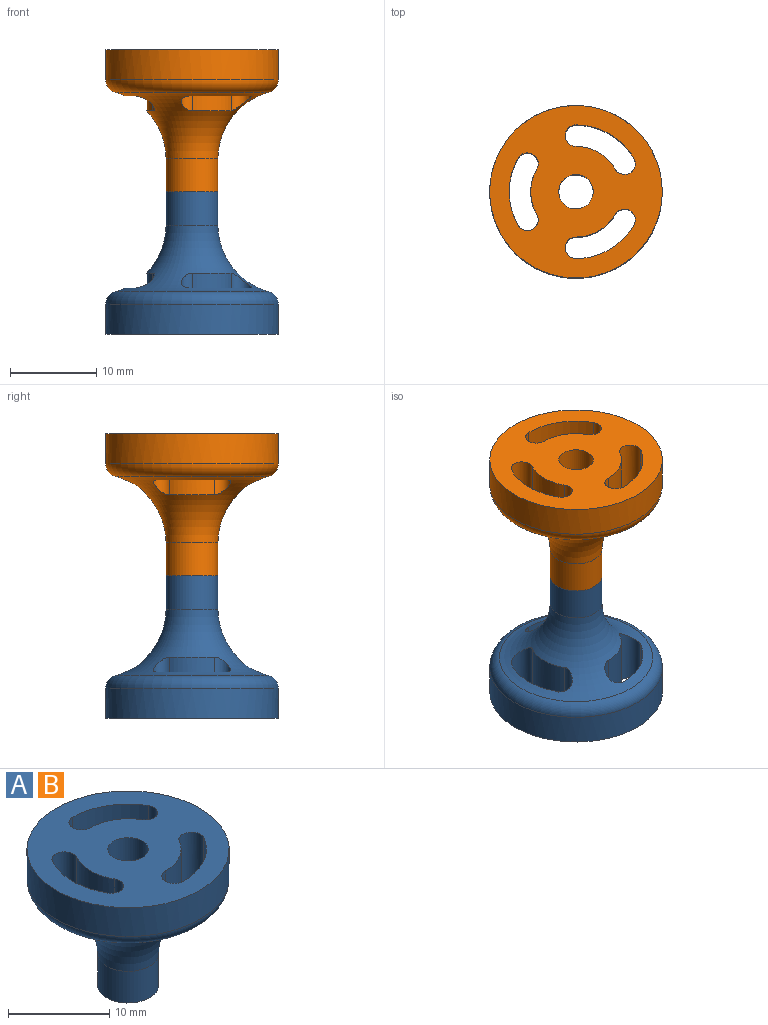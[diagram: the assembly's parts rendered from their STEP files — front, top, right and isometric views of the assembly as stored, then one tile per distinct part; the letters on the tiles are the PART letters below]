
ASSEMBLY  parts=2 mates=1
PART A: 19 faces, bbox 23.8x23.8x16.5 mm
  f0: cylinder r=7.75mm len=6.71mm, axis (0,0,1), area 43.5mm2, adj f1,f9,f14,f18
  f1: cylinder r=1.25mm len=7.1mm, axis (0,0,1), area 23.9mm2, adj f0,f2,f14,f18
  f2: cylinder r=5.25mm len=7.1mm, axis (0,0,1), area 39.1mm2, adj f1,f9,f14,f18
  f3: cylinder r=1.25mm len=7.1mm, axis (0,0,1), area 23.9mm2, adj f4,f10,f14,f18
  f4: cylinder r=7.75mm len=6.71mm, axis (0,0,1), area 43.5mm2, adj f3,f5,f14,f18
  f5: cylinder r=1.25mm len=7.1mm, axis (0,0,1), area 23.9mm2, adj f4,f10,f14,f18
  f6: cylinder r=7.75mm len=7.75mm, axis (0,0,1), area 43.5mm2, adj f7,f12,f14,f18
  f7: cylinder r=1.25mm len=7.1mm, axis (0,0,1), area 23.9mm2, adj f6,f8,f14,f18
  f8: cylinder r=5.25mm len=7.1mm, axis (0,0,1), area 39.1mm2, adj f7,f12,f14,f18
  f9: cylinder r=1.25mm len=7.1mm, axis (0,0,1), area 23.9mm2, adj f0,f2,f14,f18
  f10: cylinder r=5.25mm len=7.1mm, axis (0,0,1), area 39.1mm2, adj f3,f5,f14,f18
  f11: cylinder r=10mm len=20mm, axis (0,0,1), area 219.9mm2, adj f14,f17
  f12: cylinder r=1.25mm len=7.1mm, axis (0,0,1), area 23.9mm2, adj f6,f8,f14,f18
  f13: cylinder r=2mm len=16.5mm, axis (0,0,1), area 207.3mm2, adj f14,f16
  f14: plane 20x20mm, normal (0,0,1), area 235.8mm2, adj f0,f1,f2,f3,f4,f5,f6,f7
  f15: cylinder r=3mm len=6mm, axis (0,0,1), area 72.3mm2, adj f16,f18
  f16: plane 6x6mm, normal (0,0,-1), area 15.7mm2, adj f13,f15
  f17: torus R=8.5mm, axis (0,0,-1), area 118.1mm2, adj f11,f18
  f18: torus R=11mm, axis (0,0,-1), area 253.2mm2, adj f0,f1,f2,f3,f4,f5,f6,f7
PART B: same geometry as A
PLACE A rot(axis=(1,0,0),180deg) t=(1.13,-1.54,-30.78)mm
PLACE B t=(1.13,-1.54,6.22)mm
MATE revolute A.f13 <-> B.f13  axis (0,0,1) through (1.13,-1.54,-12.28)mm
